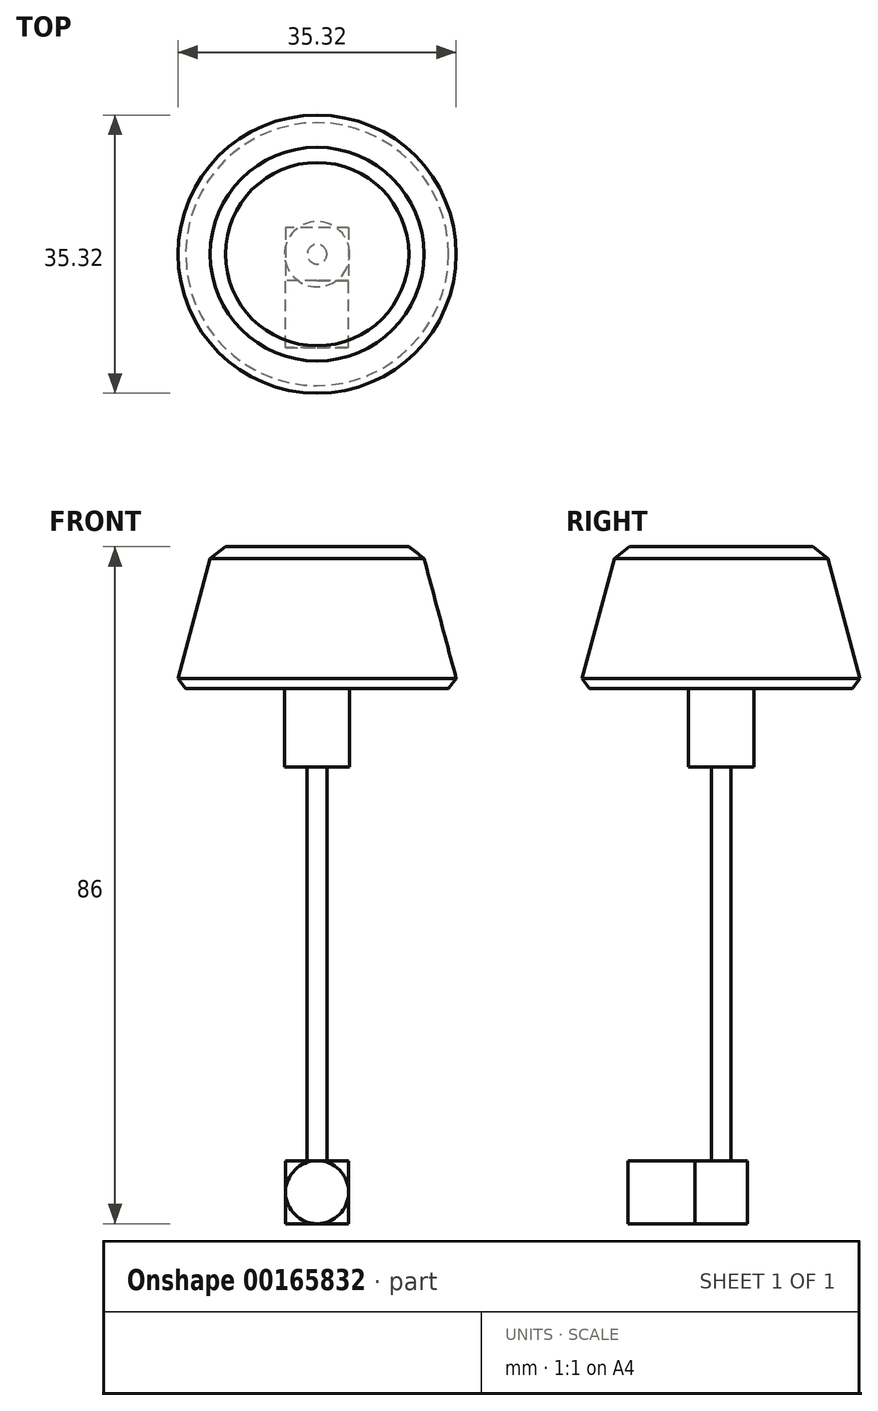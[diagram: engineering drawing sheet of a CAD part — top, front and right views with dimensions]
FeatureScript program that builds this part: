
annotation { "Feature Type Name" : "Feature", "Feature Type Description" : "" }
export const myFeature = defineFeature(function(context is Context, id is Id, definition is map)
    precondition{}
    {
        {
            var Q0;
            Q0=qCreatedBy(makeId("Front.planeOp"),FACE);
            var sketch = newSketch(context, id + "F0", { "sketchPlane" : qUnion([Q0])});
            skCircle(sketch, "E0", {"center": v(0, 0) * mm, "radius": 4 * mm});
            skSolve(sketch);
        }
        {
            var Q0;
            Q0 = qSketchRegion(id + "F0", true);
            extrude(context, id + "F1", {"entities" : qUnion([Q0]), "endBound" : BoundingType.SYMMETRIC, "depth" : 8.5 * mm});
        }
        {
            var Q0;
            Q0=makeQuery(id+"F1.opExtrude","CAP_FACE",FACE,{"disambiguationData":[OSD([sQuery(id+"F0.wireOp",EDGE,"E0")])],"isStart":true});
            var sketch = newSketch(context, id + "F2", { "sketchPlane" : qUnion([Q0])});
            skLineSegment(sketch, "E1.bottom", {"start": v(-4, -4) * mm, "end": v(4, -4) * mm});
            skLineSegment(sketch, "E1.top", {"start": v(-4, 4) * mm, "end": v(4, 4) * mm});
            skLineSegment(sketch, "E1.left", {"start": v(-4, -4) * mm, "end": v(-4, 4) * mm});
            skLineSegment(sketch, "E1.right", {"start": v(4, -4) * mm, "end": v(4, 4) * mm});
            skPoint(sketch, "E1.middle", {"position": v(0, 0) * mm});
            skSolve(sketch);
        }
        {
            var Q0;
            Q0 = qSketchRegion(id + "F2", true);
            extrude(context, id + "F3", {"entities" : qUnion([Q0]), "operationType" : NewBodyOperationType.ADD, "depth" : 6.7 * mm});
        }
        {
            var Q0;
            Q0=makeQuery(id+"F3.opExtrude","SWEPT_FACE",FACE,{"disambiguationData":[OSD([sQuery(id+"F2.wireOp",EDGE,"E1.top")])]});
            var sketch = newSketch(context, id + "F4", { "sketchPlane" : qUnion([Q0])});
            skCircle(sketch, "E2", {"center": v(0, 7.6) * mm, "radius": 1.25 * mm});
            skLineSegment(sketch, "E3", {"start": v(0, 10.95) * mm, "end": v(0, 4.25) * mm, "construction": true});
            skSolve(sketch);
        }
        {
            var Q0;
            Q0 = qSketchRegion(id + "F4", true);
            extrude(context, id + "F5", {"entities" : qUnion([Q0]), "operationType" : NewBodyOperationType.ADD, "depth" : 50 * mm});
        }
        {
            var Q0;
            Q0=makeQuery(id+"F5.opExtrude","CAP_FACE",FACE,{"disambiguationData":[OSD([sQuery(id+"F4.wireOp",EDGE,"E2")])],"isStart":false});
            var sketch = newSketch(context, id + "F6", { "sketchPlane" : qUnion([Q0])});
            skCircle(sketch, "E4", {"center": v(0, 7.6) * mm, "radius": 4.15 * mm});
            skSolve(sketch);
        }
        {
            var Q0;
            Q0 = qSketchRegion(id + "F6", true);
            extrude(context, id + "F7", {"entities" : qUnion([Q0]), "operationType" : NewBodyOperationType.ADD, "depth" : 10 * mm});
        }
        {
            var Q0;
            Q0=makeQuery(id+"F7.opExtrude","CAP_FACE",FACE,{"disambiguationData":[OSD([sQuery(id+"F6.wireOp",EDGE,"E4")])],"isStart":false});
            var sketch = newSketch(context, id + "F8", { "sketchPlane" : qUnion([Q0])});
            skCircle(sketch, "E5", {"center": v(0, 7.6) * mm, "radius": 18 * mm});
            skSolve(sketch);
        }
        {
            var Q0;
            Q0=makeQuery(id+"F8.imprint","IMPRINT",FACE,{"disambiguationData":[TD([[makeQuery(id+"F8.imprint","IMPRINT",EDGE,{"derivedFrom":sQuery(id+"F8.wireOp",EDGE,"E5")}),1.0]])]});
            var Q1;
            Q1=makeQuery(id+"F8.imprint","IMPRINT",FACE,{"disambiguationData":[TD([[makeQuery(id+"F8.imprint","IMPRINT",EDGE,{"derivedFrom":makeQuery(id+"F7.opExtrude","CAP_EDGE",EDGE,{"disambiguationData":[OSD([sQuery(id+"F6.wireOp",EDGE,"E4")])],"isStart":false})}),1.0]])]});
            extrude(context, id + "F9", {"entities" : qUnion([Q0, Q1]), "operationType" : NewBodyOperationType.ADD, "depth" : 18 * mm, "hasDraft" : true, "draftAngle" : 15 * degree, "draftPullDirection" : true});
        }
        {
            var Q0;
            Q0=makeQuery(id+"F9.opExtrude","CAP_EDGE",EDGE,{"disambiguationData":[OSD([sQuery(id+"F8.wireOp",EDGE,"E5")])],"isStart":true});
            chamfer(context, id + "F10", {"entities" : qUnion([Q0]), "width" : 1 * mm, "tangentPropagation" : true});
        }
        {
            var Q0;
            Q0=makeQuery(id+"F9.opExtrude","CAP_EDGE",EDGE,{"disambiguationData":[OSD([sQuery(id+"F8.wireOp",EDGE,"E5")])],"isStart":false});
            chamfer(context, id + "F11", {"entities" : qUnion([Q0]), "width" : 2 * mm, "tangentPropagation" : true});
        }
    });
